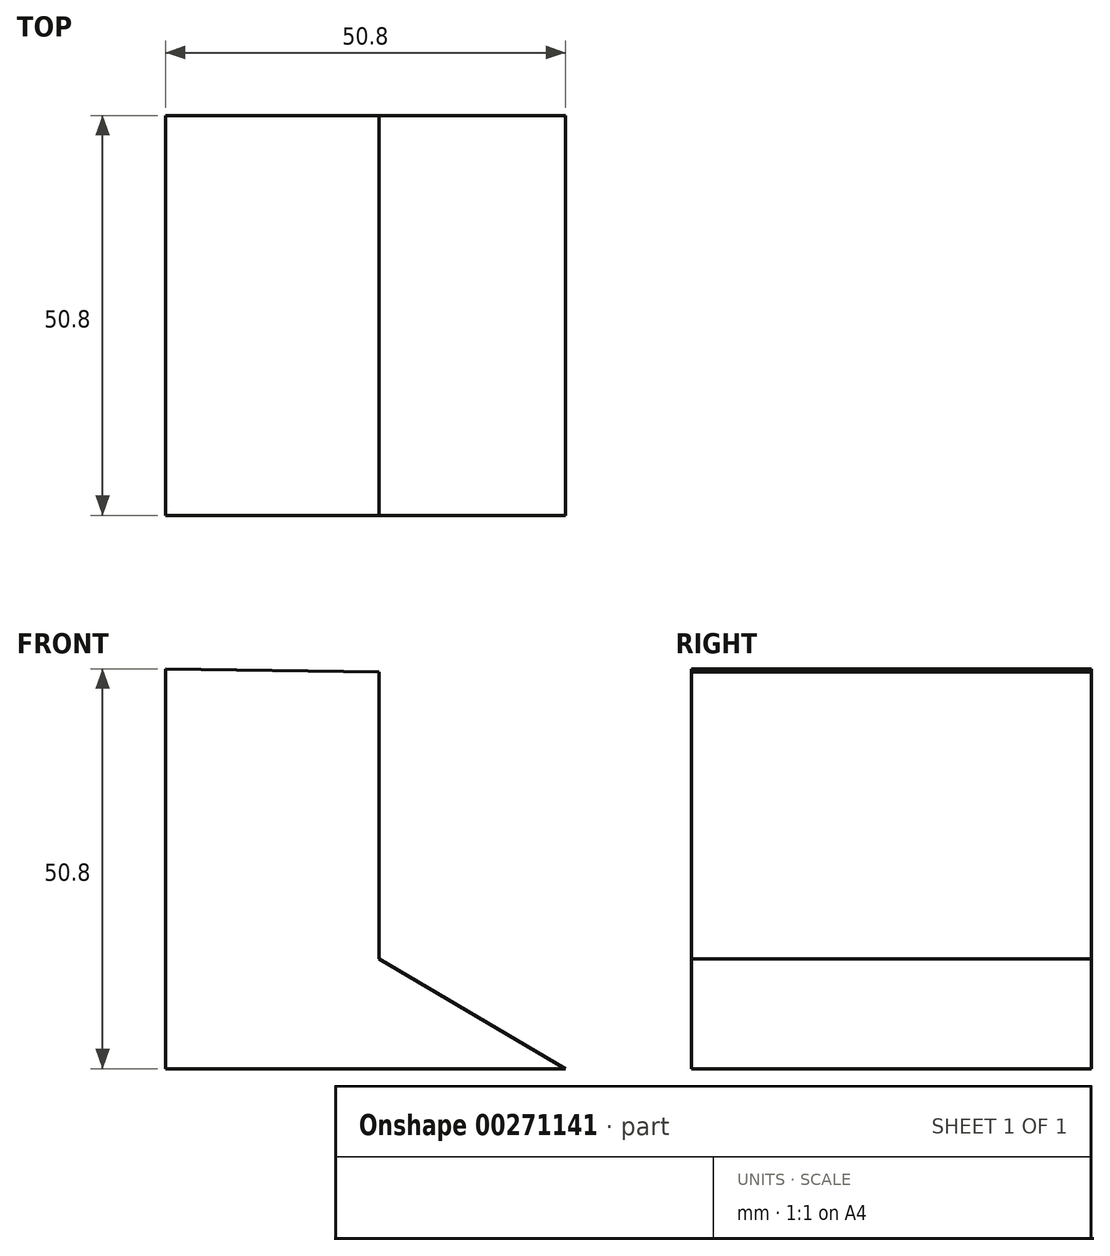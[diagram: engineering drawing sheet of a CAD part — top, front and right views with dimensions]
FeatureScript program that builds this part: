
annotation { "Feature Type Name" : "Feature", "Feature Type Description" : "" }
export const myFeature = defineFeature(function(context is Context, id is Id, definition is map)
    precondition{}
    {
        {
            var Q0;
            Q0=qCreatedBy(makeId("Front.planeOp"),FACE);
            var sketch = newSketch(context, id + "F0", { "sketchPlane" : qUnion([Q0])});
            skLineSegment(sketch, "E0", {"start": v(-46.02, 59.01) * mm, "end": v(-46.02, 8.21) * mm});
            skLineSegment(sketch, "E1", {"start": v(-46.02, 8.21) * mm, "end": v(4.78, 8.21) * mm});
            skLineSegment(sketch, "E2", {"start": v(4.78, 8.21) * mm, "end": v(-18.9, 22.15) * mm});
            skLineSegment(sketch, "E3", {"start": v(-18.9, 22.15) * mm, "end": v(-18.9, 58.62) * mm});
            skLineSegment(sketch, "E4", {"start": v(-18.9, 58.62) * mm, "end": v(-46.02, 59.01) * mm});
            skSolve(sketch);
        }
        {
            var Q0;
            Q0 = qSketchRegion(id + "F0", true);
            extrude(context, id + "F1", {"entities" : qUnion([Q0]), "depth" : 50.8 * mm});
        }
    });
